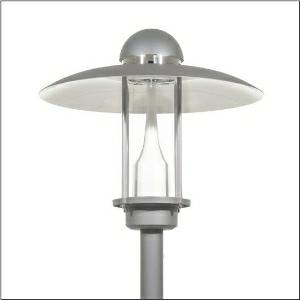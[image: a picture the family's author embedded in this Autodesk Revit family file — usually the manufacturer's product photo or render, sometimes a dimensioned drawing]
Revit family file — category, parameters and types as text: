
# Revit family: city-light_elegance_iq___pl1_2s_5xa5265jf14h000022_4ac6
name_source: partatom
category: Lighting Fixtures
units: mm (PartAtom-declared; Revit-internal decimal feet)

## family parameters
Cut with Voids When Loaded = No
Host = Face
Light Source = No
Part Type = Normal
Room Calculation Point = No
Round Connector Dimension = Use Diameter
Shared = No

## types (1)
- --- (1 x LED, 2840 lm, 19.3 W, 3000K)
    Apparent Load = 19 VA
    CIE Flux Codes = 24 63 94 98 100
    Color Rendering = 70
    Color Temperature = 3000K
    Default Elevation = 1800 mm
    Description = City-Light Elegance iQ, mast luminaire, Module 540 iQ-SR, primary light control with 3 zone facetted reflector, of plastic, silver coated, highly specular, structured, primary optical cover: cover, of PMMA, transparent, light distribution: PL1.2s, light emission: direct distribution, primary light characteristic: symmetric, installation type: post-top, LED, High Power LED, rated luminous flux: 2.840lm, luminous efficacy: 147lm/W, light colour: 730, colour temperature: 3000K, control gear: iQ Street-Remote, control: Street-Remote, Auto-Match, Temp-Guard, Lumen-Switch, Night-Set, Smart-Wire, Light-Fading, Desk-Remote (wireless, voltage-free reading and setting of iQ features in the workshop via application-optimized NFC function/RFID function), optimised constant luminous flux control (CLO 2.0), pre-setting: logarithmic dimming characteristic, mains connection: 230..240V, AC, 50/60Hz, connection cable pre-assembled, cable length: 5,5m, wiring characteristics: H07RN-F, start of lifetime: 19W, end of service life: 21W, reduction: 10W, luminaire housing, upper part, of aluminium, coated, Siteco® metallic grey (DB 702S), diameter: 750mm, height: 675mm, spigot size: d x l = 76 x 70mm (post-top) | with reducer (optional accessory) 60 x 70mm, mounting height: 3..5m, post-top mast mounting element, of diecast aluminium, coated, Siteco® metallic grey (DB 702S), Module 540 iQ-SR, traffic white (RAL 9016), equipment: standard, protection rating (complete): IP65, insulation class (complete): insulation class II (safety insulation), certification: CE, ENEC, VDE, packaging unit: 1 piece

Light Distribution: PL1.2s
    Height = 675 mm
    Lamp = 1 x LED
    Lamp Light Flux = 2840 lm
    Lamp Power = 19.3 W
    Lamp count = 1
    Length = 750 mm
    Luminous efficacy = 147 lm/W
    Manufacturer = Siteco
    ModVariant = No
    Model = 5XA5265JF14H000022
    Number of Poles = 1
    OnlyDefault = Yes
    Power Factor = 1
    Product Name = City-Light Elegance iQ | PL1.2s
    Product group = mast luminaire | pylon top
    ProductGroupID = 6100
    Protection Class = Protection class II
    Protection Degree = IP 65
    RLX_Detail_Level = 1
    RLX_Emergency_Light_Flux = 0 lm
    RLX_Emergency_Type = 0
    RLX_Emergency_Type_DB = No
    RlxData = <blob elided: 33677 chars, md5=618fc64d>
    Socket = socket
    Standby Power = 0 W
    System Light Flux = 2840 lm
    System Power = 19 W
    Type Comments = factory setting: luminous flux: 100 % | dim-lin: 254 | 403 mA
    Type Image = l_1006912.jpg
    URL = http://relux.com
    VarID = @adj_166783
    Voltage = 0 V
    Weight = 0.00 kg
    Width = 0 mm  [stored 0 ft]

note: [stored X ft] marks values corroborated as IEEE doubles in the binary element streams (Revit-internal decimal feet)

## geometry (parser evidence)
native form markers: Blend x4, Sweep x9
no freeform markers — native parametric forms only
